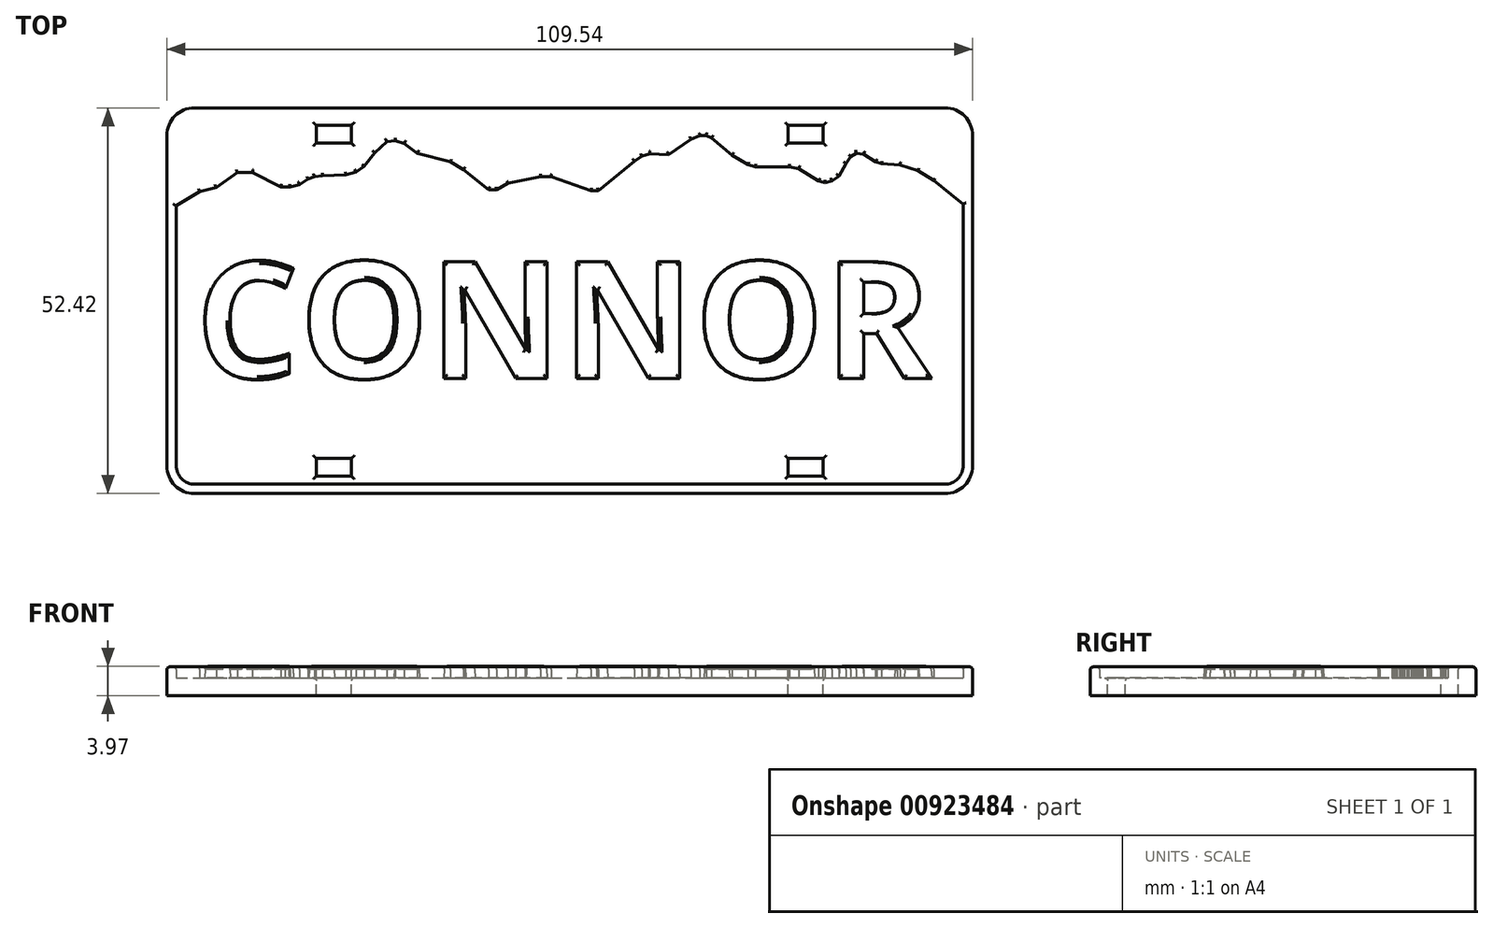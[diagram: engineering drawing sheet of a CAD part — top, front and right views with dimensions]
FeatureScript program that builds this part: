
annotation { "Feature Type Name" : "Feature", "Feature Type Description" : "" }
export const myFeature = defineFeature(function(context is Context, id is Id, definition is map)
    precondition{}
    {
        {
            var Q0;
            Q0=qCreatedBy(makeId("Top.planeOp"),FACE);
            var sketch = newSketch(context, id + "F0", { "sketchPlane" : qUnion([Q0])});
            skLineSegment(sketch, "E0", {"start": v(54.77, -22.46) * mm, "end": v(54.77, 22.46) * mm});
            skArc(sketch, "E1", {"start": v(54.77, 22.46) * mm, "mid": v(53.68, 25.11) * mm, "end": v(51.02, 26.21) * mm});
            skLineSegment(sketch, "E2", {"start": v(51.02, 26.21) * mm, "end": v(-51.02, 26.21) * mm});
            skArc(sketch, "E3", {"start": v(-51.02, 26.21) * mm, "mid": v(-53.68, 25.11) * mm, "end": v(-54.77, 22.46) * mm});
            skLineSegment(sketch, "E4", {"start": v(-54.77, 22.46) * mm, "end": v(-54.77, -22.46) * mm});
            skArc(sketch, "E5", {"start": v(-54.77, -22.46) * mm, "mid": v(-53.54, -25.24) * mm, "end": v(-50.64, -26.2) * mm});
            skLineSegment(sketch, "E6", {"start": v(-50.64, -26.2) * mm, "end": v(51.04, -26.2) * mm});
            skArc(sketch, "E7", {"start": v(51.02, -26.21) * mm, "mid": v(53.68, -25.11) * mm, "end": v(54.77, -22.46) * mm});
            skLineSegment(sketch, "E8", {"start": v(-54.77, 12.13) * mm, "end": v(-50.31, 14.84) * mm});
            skLineSegment(sketch, "E9", {"start": v(-50.31, 14.84) * mm, "end": v(-48.06, 15.4) * mm});
            skLineSegment(sketch, "E10", {"start": v(-48.06, 15.4) * mm, "end": v(-45.2, 17.44) * mm});
            skLineSegment(sketch, "E11", {"start": v(-45.2, 17.44) * mm, "end": v(-43.14, 17.44) * mm});
            skLineSegment(sketch, "E12", {"start": v(-43.14, 17.44) * mm, "end": v(-39.3, 15.5) * mm});
            skLineSegment(sketch, "E13", {"start": v(-39.3, 15.5) * mm, "end": v(-38.03, 15.49) * mm});
            skLineSegment(sketch, "E14", {"start": v(-38.03, 15.49) * mm, "end": v(-36.75, 15.8) * mm});
            skLineSegment(sketch, "E15", {"start": v(-36.75, 15.8) * mm, "end": v(-35.57, 16.54) * mm});
            skLineSegment(sketch, "E16", {"start": v(-35.57, 16.54) * mm, "end": v(-34.73, 16.88) * mm});
            skLineSegment(sketch, "E17", {"start": v(-34.73, 16.88) * mm, "end": v(-33.6, 17.01) * mm});
            skLineSegment(sketch, "E18", {"start": v(-33.6, 17.01) * mm, "end": v(-30.43, 17.11) * mm});
            skLineSegment(sketch, "E19", {"start": v(-29.05, 17.5) * mm, "end": v(-27.98, 18.27) * mm});
            skLineSegment(sketch, "E20", {"start": v(-27.98, 18.27) * mm, "end": v(-26.53, 20.14) * mm});
            skLineSegment(sketch, "E21", {"start": v(-26.53, 20.14) * mm, "end": v(-24.88, 21.63) * mm});
            skLineSegment(sketch, "E22", {"start": v(-24.88, 21.63) * mm, "end": v(-23.73, 21.77) * mm});
            skLineSegment(sketch, "E23", {"start": v(-22.5, 21.4) * mm, "end": v(-20.72, 20.04) * mm});
            skLineSegment(sketch, "E24", {"start": v(-16.23, 18.87) * mm, "end": v(-14.45, 17.85) * mm});
            skLineSegment(sketch, "E25", {"start": v(-14.45, 17.85) * mm, "end": v(-11.02, 15.1) * mm});
            skLineSegment(sketch, "E26", {"start": v(-11.02, 15.1) * mm, "end": v(-9.93, 15.1) * mm});
            skLineSegment(sketch, "E27", {"start": v(-9.93, 15.1) * mm, "end": v(-8.4, 15.96) * mm});
            skLineSegment(sketch, "E28", {"start": v(-8.4, 15.96) * mm, "end": v(-3.94, 16.85) * mm});
            skLineSegment(sketch, "E29", {"start": v(-3.94, 16.85) * mm, "end": v(-2.54, 16.85) * mm});
            skLineSegment(sketch, "E30", {"start": v(-2.54, 16.85) * mm, "end": v(2.9, 14.97) * mm});
            skLineSegment(sketch, "E31", {"start": v(2.9, 14.97) * mm, "end": v(3.92, 14.97) * mm});
            skLineSegment(sketch, "E32", {"start": v(3.92, 14.97) * mm, "end": v(8.8, 18.97) * mm});
            skLineSegment(sketch, "E33", {"start": v(8.8, 18.97) * mm, "end": v(9.82, 19.64) * mm});
            skLineSegment(sketch, "E34", {"start": v(9.82, 19.64) * mm, "end": v(10.9, 19.97) * mm});
            skLineSegment(sketch, "E35", {"start": v(10.9, 19.97) * mm, "end": v(13.43, 19.86) * mm});
            skLineSegment(sketch, "E36", {"start": v(16.5, 21.96) * mm, "end": v(17.71, 22.42) * mm});
            skLineSegment(sketch, "E37", {"start": v(17.71, 22.42) * mm, "end": v(18.56, 22.45) * mm});
            skLineSegment(sketch, "E38", {"start": v(18.56, 22.45) * mm, "end": v(19.28, 22.13) * mm});
            skLineSegment(sketch, "E39", {"start": v(19.28, 22.13) * mm, "end": v(22.05, 19.8) * mm});
            skLineSegment(sketch, "E40", {"start": v(22.05, 19.8) * mm, "end": v(24.2, 18.5) * mm});
            skLineSegment(sketch, "E41", {"start": v(24.2, 18.5) * mm, "end": v(25.23, 18.2) * mm});
            skLineSegment(sketch, "E42", {"start": v(25.23, 18.2) * mm, "end": v(29.85, 18.2) * mm});
            skLineSegment(sketch, "E43", {"start": v(29.85, 18.2) * mm, "end": v(31.13, 17.95) * mm});
            skLineSegment(sketch, "E44", {"start": v(31.13, 17.95) * mm, "end": v(33.84, 16.27) * mm});
            skLineSegment(sketch, "E45", {"start": v(33.84, 16.27) * mm, "end": v(34.73, 16.06) * mm});
            skLineSegment(sketch, "E46", {"start": v(34.73, 16.06) * mm, "end": v(35.67, 16.3) * mm});
            skLineSegment(sketch, "E47", {"start": v(35.67, 16.3) * mm, "end": v(36.58, 16.95) * mm});
            skLineSegment(sketch, "E48", {"start": v(36.58, 16.95) * mm, "end": v(37.58, 18.67) * mm});
            skLineSegment(sketch, "E49", {"start": v(38.22, 19.58) * mm, "end": v(38.96, 20.06) * mm});
            skLineSegment(sketch, "E50", {"start": v(38.96, 20.06) * mm, "end": v(39.94, 19.92) * mm});
            skLineSegment(sketch, "E51", {"start": v(41.58, 18.88) * mm, "end": v(42.4, 18.61) * mm});
            skLineSegment(sketch, "E52", {"start": v(42.4, 18.61) * mm, "end": v(44.9, 18.47) * mm});
            skLineSegment(sketch, "E53", {"start": v(44.9, 18.47) * mm, "end": v(47.31, 17.68) * mm});
            skLineSegment(sketch, "E54", {"start": v(47.31, 17.68) * mm, "end": v(49.47, 16.33) * mm});
            skLineSegment(sketch, "E55", {"start": v(49.47, 16.33) * mm, "end": v(51.88, 14.42) * mm});
            skLineSegment(sketch, "E56", {"start": v(51.88, 14.42) * mm, "end": v(53.78, 12.92) * mm});
            skLineSegment(sketch, "E57", {"start": v(53.78, 12.92) * mm, "end": v(54.77, 12.06) * mm});
            skLineSegment(sketch, "E58", {"start": v(-20.72, 20.04) * mm, "end": v(-16.23, 18.87) * mm});
            skLineSegment(sketch, "E59", {"start": v(16.5, 21.96) * mm, "end": v(13.43, 19.86) * mm});
            skLineSegment(sketch, "E60", {"start": v(-22.5, 21.4) * mm, "end": v(-23.73, 21.77) * mm});
            skLineSegment(sketch, "E61", {"start": v(-29.05, 17.5) * mm, "end": v(-30.43, 17.11) * mm});
            skLineSegment(sketch, "E62", {"start": v(37.58, 18.67) * mm, "end": v(38.22, 19.58) * mm});
            skLineSegment(sketch, "E63", {"start": v(41.58, 18.88) * mm, "end": v(39.94, 19.92) * mm});
            skSolve(sketch);
        }
        {
            var Q0;
            Q0=qCreatedBy(makeId("Top.planeOp"),FACE);
            var sketch = newSketch(context, id + "F1", { "sketchPlane" : qUnion([Q0])});
            skLineSegment(sketch, "E64", {"start": v(54.77, -22.46) * mm, "end": v(54.77, 22.46) * mm});
            skArc(sketch, "E65", {"start": v(54.77, 22.46) * mm, "mid": v(53.68, 25.11) * mm, "end": v(51.02, 26.21) * mm});
            skLineSegment(sketch, "E66", {"start": v(51.02, 26.21) * mm, "end": v(-51.02, 26.21) * mm});
            skArc(sketch, "E67", {"start": v(-51.02, 26.21) * mm, "mid": v(-53.68, 25.11) * mm, "end": v(-54.77, 22.46) * mm});
            skLineSegment(sketch, "E68", {"start": v(-54.77, 22.46) * mm, "end": v(-54.77, -22.46) * mm});
            skArc(sketch, "E69", {"start": v(-54.77, -22.46) * mm, "mid": v(-53.68, -25.11) * mm, "end": v(-51.02, -26.21) * mm});
            skLineSegment(sketch, "E70", {"start": v(-51.02, -26.21) * mm, "end": v(51.02, -26.21) * mm});
            skArc(sketch, "E71", {"start": v(51.02, -26.21) * mm, "mid": v(53.68, -25.11) * mm, "end": v(54.77, -22.46) * mm});
            skLineSegment(sketch, "E72.0", {"start": v(50.96, 24.94) * mm, "end": v(-50.96, 24.94) * mm, "construction": true});
            skLineSegment(sketch, "E72.1", {"start": v(53.5, -22.4) * mm, "end": v(53.5, 22.4) * mm, "construction": true});
            skLineSegment(sketch, "E72.2", {"start": v(-50.96, -24.94) * mm, "end": v(50.96, -24.94) * mm, "construction": true});
            skLineSegment(sketch, "E72.3", {"start": v(-53.5, 22.4) * mm, "end": v(-53.5, -22.4) * mm, "construction": true});
            skPoint(sketch, "E73.visualSharp", {"position": v(-53.5, 24.94) * mm});
            skArc(sketch, "E73.filletArc", {"start": v(-50.96, 24.94) * mm, "mid": v(-52.76, 24.2) * mm, "end": v(-53.5, 22.4) * mm, "construction": true});
            skPoint(sketch, "E74.visualSharp", {"position": v(-53.5, -24.94) * mm});
            skArc(sketch, "E74.filletArc", {"start": v(-53.5, -22.4) * mm, "mid": v(-52.76, -24.2) * mm, "end": v(-50.96, -24.94) * mm, "construction": true});
            skPoint(sketch, "E75.visualSharp", {"position": v(53.5, -24.94) * mm});
            skArc(sketch, "E75.filletArc", {"start": v(50.96, -24.94) * mm, "mid": v(52.76, -24.2) * mm, "end": v(53.5, -22.4) * mm, "construction": true});
            skPoint(sketch, "E76.visualSharp", {"position": v(53.5, 24.94) * mm});
            skArc(sketch, "E76.filletArc", {"start": v(53.5, 22.4) * mm, "mid": v(52.76, 24.2) * mm, "end": v(50.96, 24.94) * mm, "construction": true});
            skSolve(sketch);
        }
        {
            var Q0;
            {var subQ3=sQuery(id+"F0.wireOp",EDGE,"E1");Q0=makeQuery(id+"F0.imprint","IMPRINT",FACE,{"disambiguationData":[TD([[makeQuery(id+"F0.imprint","IMPRINT",EDGE,{"derivedFrom":subQ3}),1.0]])]});}
            extrude(context, id + "F2", {"entities" : qUnion([Q0]), "depth" : 1.52 * mm, "offsetDistance" : 25.4 * mm});
        }
        {
            var Q0;
            Q0=qSketchRegion(id+"F1",true);
            extrude(context, id + "F3", {"entities" : qUnion([Q0]), "operationType" : NewBodyOperationType.ADD, "oppositeDirection" : true, "depth" : 2.38 * mm, "offsetDistance" : 25.4 * mm});
        }
        {
            var Q0;
            {var subQ58=sQuery(id+"F0.wireOp",EDGE,"E0");var subQ59=sQuery(id+"F1.wireOp",EDGE,"E64");var subQ60=sQuery(id+"F1.wireOp",EDGE,"E65");var subQ61=sQuery(id+"F1.wireOp",EDGE,"E68");var subQ62=sQuery(id+"F1.wireOp",EDGE,"E69");var subQ63=sQuery(id+"F1.wireOp",EDGE,"E70");var subQ64=sQuery(id+"F1.wireOp",EDGE,"E71");Q0=makeQuery(id+"F3.boolean.opBoolean","SPLIT",FACE,{"disambiguationData":[TD([makeQuery(id+"F2.opExtrude","SWEPT_FACE",FACE,{"disambiguationData":[OSD([subQ58])]})])],"derivedFrom":makeQuery(id+"F3.opExtrude","CAP_FACE",FACE,{"disambiguationData":[OSD([subQ59,subQ60,sQuery(id+"F1.wireOp",EDGE,"E66"),sQuery(id+"F1.wireOp",EDGE,"E67"),subQ61,subQ62,subQ63,subQ64])],"isStart":true})});}
            var sketch = newSketch(context, id + "F4", { "sketchPlane" : qUnion([Q0])});
            skLineSegment(sketch, "E77", {"start": v(54.77, -22.46) * mm, "end": v(54.77, 12.06) * mm});
            skLineSegment(sketch, "E78", {"start": v(-54.77, 12.13) * mm, "end": v(-54.77, -22.46) * mm});
            skArc(sketch, "E79", {"start": v(-54.77, -22.46) * mm, "mid": v(-53.68, -25.11) * mm, "end": v(-51.02, -26.21) * mm});
            skLineSegment(sketch, "E80", {"start": v(-51.02, -26.21) * mm, "end": v(51.02, -26.21) * mm});
            skArc(sketch, "E81", {"start": v(51.02, -26.21) * mm, "mid": v(53.68, -25.11) * mm, "end": v(54.77, -22.46) * mm});
            skLineSegment(sketch, "E82.1", {"start": v(53.5, -22.4) * mm, "end": v(53.5, 13.14) * mm});
            skLineSegment(sketch, "E82.2", {"start": v(-50.96, -24.94) * mm, "end": v(50.96, -24.94) * mm});
            skLineSegment(sketch, "E82.3", {"start": v(-53.5, 12.9) * mm, "end": v(-53.5, -22.4) * mm});
            skPoint(sketch, "E83.visualSharp", {"position": v(-53.5, 24.94) * mm});
            skPoint(sketch, "E84.visualSharp", {"position": v(-53.5, -24.94) * mm});
            skArc(sketch, "E84.filletArc", {"start": v(-53.5, -22.4) * mm, "mid": v(-52.76, -24.2) * mm, "end": v(-50.96, -24.94) * mm});
            skPoint(sketch, "E85.visualSharp", {"position": v(53.5, -24.94) * mm});
            skArc(sketch, "E85.filletArc", {"start": v(50.96, -24.94) * mm, "mid": v(52.76, -24.2) * mm, "end": v(53.5, -22.4) * mm});
            skPoint(sketch, "E86.visualSharp", {"position": v(53.5, 24.94) * mm});
            skLineSegment(sketch, "E87", {"start": v(-54.77, 12.13) * mm, "end": v(-53.5, 12.9) * mm});
            skLineSegment(sketch, "E88", {"start": v(53.5, 13.14) * mm, "end": v(53.78, 12.92) * mm});
            skLineSegment(sketch, "E89", {"start": v(53.78, 12.92) * mm, "end": v(54.77, 12.06) * mm});
            skSolve(sketch);
        }
        {
            var Q0;
            Q0=qSketchRegion(id+"F4",true);
            extrude(context, id + "F5", {"entities" : qUnion([Q0]), "operationType" : NewBodyOperationType.ADD, "depth" : 1.52 * mm, "offsetDistance" : 25.4 * mm});
        }
        {
            var Q0;
            Q0=makeQuery(id+"F5.boolean.opBoolean","MERGE",FACE,{"derivedFrom":[makeQuery(id+"F2.opExtrude","CAP_FACE",FACE,{"disambiguationData":[OSD([sQuery(id+"F0.wireOp",EDGE,"E0"),sQuery(id+"F0.wireOp",EDGE,"E1"),sQuery(id+"F0.wireOp",EDGE,"E2"),sQuery(id+"F0.wireOp",EDGE,"E3"),sQuery(id+"F0.wireOp",EDGE,"E4"),sQuery(id+"F0.wireOp",EDGE,"E8"),sQuery(id+"F0.wireOp",EDGE,"E9"),sQuery(id+"F0.wireOp",EDGE,"E10"),sQuery(id+"F0.wireOp",EDGE,"E11"),sQuery(id+"F0.wireOp",EDGE,"E12"),sQuery(id+"F0.wireOp",EDGE,"E13"),sQuery(id+"F0.wireOp",EDGE,"E14"),sQuery(id+"F0.wireOp",EDGE,"E15"),sQuery(id+"F0.wireOp",EDGE,"E16"),sQuery(id+"F0.wireOp",EDGE,"E17"),sQuery(id+"F0.wireOp",EDGE,"E18"),sQuery(id+"F0.wireOp",EDGE,"7b9f405e-0691-426e-9c9e-a5372cf0836a"),sQuery(id+"F0.wireOp",EDGE,"E19"),sQuery(id+"F0.wireOp",EDGE,"E20"),sQuery(id+"F0.wireOp",EDGE,"E21"),sQuery(id+"F0.wireOp",EDGE,"E22"),sQuery(id+"F0.wireOp",EDGE,"b3dec5b1-662c-4d50-a13c-af7b7760114a"),sQuery(id+"F0.wireOp",EDGE,"E23"),sQuery(id+"F0.wireOp",EDGE,"4d9ee76e-0833-4cdc-b1a8-2d4ce76e6521"),sQuery(id+"F0.wireOp",EDGE,"E24"),sQuery(id+"F0.wireOp",EDGE,"E25"),sQuery(id+"F0.wireOp",EDGE,"E26"),sQuery(id+"F0.wireOp",EDGE,"E27"),sQuery(id+"F0.wireOp",EDGE,"E28"),sQuery(id+"F0.wireOp",EDGE,"E29"),sQuery(id+"F0.wireOp",EDGE,"E30"),sQuery(id+"F0.wireOp",EDGE,"E31"),sQuery(id+"F0.wireOp",EDGE,"E32"),sQuery(id+"F0.wireOp",EDGE,"E33"),sQuery(id+"F0.wireOp",EDGE,"E34"),sQuery(id+"F0.wireOp",EDGE,"E35"),sQuery(id+"F0.wireOp",EDGE,"55551997-bb9e-4b94-90c5-def3cb147476"),sQuery(id+"F0.wireOp",EDGE,"E36"),sQuery(id+"F0.wireOp",EDGE,"E37"),sQuery(id+"F0.wireOp",EDGE,"E38"),sQuery(id+"F0.wireOp",EDGE,"E39"),sQuery(id+"F0.wireOp",EDGE,"E40"),sQuery(id+"F0.wireOp",EDGE,"E41"),sQuery(id+"F0.wireOp",EDGE,"E42"),sQuery(id+"F0.wireOp",EDGE,"E43"),sQuery(id+"F0.wireOp",EDGE,"E44"),sQuery(id+"F0.wireOp",EDGE,"E45"),sQuery(id+"F0.wireOp",EDGE,"E46"),sQuery(id+"F0.wireOp",EDGE,"E47"),sQuery(id+"F0.wireOp",EDGE,"E48"),sQuery(id+"F0.wireOp",EDGE,"513b7cbe-d979-4e22-b277-f3c42ccdbda1"),sQuery(id+"F0.wireOp",EDGE,"E49"),sQuery(id+"F0.wireOp",EDGE,"E50"),sQuery(id+"F0.wireOp",EDGE,"0d842e13-672c-40e3-aae4-28923e78d4e0"),sQuery(id+"F0.wireOp",EDGE,"E51"),sQuery(id+"F0.wireOp",EDGE,"E52"),sQuery(id+"F0.wireOp",EDGE,"E53"),sQuery(id+"F0.wireOp",EDGE,"E54"),sQuery(id+"F0.wireOp",EDGE,"E55"),sQuery(id+"F0.wireOp",EDGE,"E56"),sQuery(id+"F0.wireOp",EDGE,"E57")])],"isStart":false}),makeQuery(id+"F5.opExtrude","CAP_FACE",FACE,{"disambiguationData":[OSD([sQuery(id+"F4.wireOp",EDGE,"E77"),sQuery(id+"F4.wireOp",EDGE,"E78"),sQuery(id+"F4.wireOp",EDGE,"E79"),sQuery(id+"F4.wireOp",EDGE,"E80"),sQuery(id+"F4.wireOp",EDGE,"E81"),sQuery(id+"F4.wireOp",EDGE,"E82.1"),sQuery(id+"F4.wireOp",EDGE,"E82.2"),sQuery(id+"F4.wireOp",EDGE,"E82.3"),sQuery(id+"F4.wireOp",EDGE,"E84.filletArc"),sQuery(id+"F4.wireOp",EDGE,"E85.filletArc"),sQuery(id+"F4.wireOp",EDGE,"E87"),sQuery(id+"F4.wireOp",EDGE,"E88"),sQuery(id+"F4.wireOp",EDGE,"E89")])],"isStart":false})]});
            var sketch = newSketch(context, id + "F6", { "sketchPlane" : qUnion([Q0])});
            skLineSegment(sketch, "E90.bottom", {"start": v(-34.45, 23.83) * mm, "end": v(-29.7, 23.83) * mm});
            skLineSegment(sketch, "E90.top", {"start": v(-34.45, 21.45) * mm, "end": v(-29.7, 21.45) * mm});
            skLineSegment(sketch, "E90.left", {"start": v(-34.45, 23.83) * mm, "end": v(-34.45, 21.45) * mm});
            skLineSegment(sketch, "E90.right", {"start": v(-29.7, 23.83) * mm, "end": v(-29.7, 21.45) * mm});
            skLineSegment(sketch, "E91", {"start": v(0, 26.21) * mm, "end": v(0, -26.21) * mm, "construction": true});
            skLineSegment(sketch, "E92.MirrorCS", {"start": v(34.45, 23.83) * mm, "end": v(34.45, 21.45) * mm});
            skLineSegment(sketch, "E93.MirrorCS", {"start": v(29.7, 23.83) * mm, "end": v(29.7, 21.45) * mm});
            skLineSegment(sketch, "E94.MirrorCS", {"start": v(34.45, 21.45) * mm, "end": v(29.7, 21.45) * mm});
            skLineSegment(sketch, "E95.MirrorCS", {"start": v(34.45, 23.83) * mm, "end": v(29.7, 23.83) * mm});
            skLineSegment(sketch, "E96", {"start": v(0, 0) * mm, "end": v(-59.23, 0) * mm, "construction": true});
            skLineSegment(sketch, "E97", {"start": v(0, 0) * mm, "end": v(56.47, 0) * mm, "construction": true});
            skLineSegment(sketch, "E98.MirrorCS", {"start": v(-34.45, -23.83) * mm, "end": v(-29.7, -23.83) * mm});
            skLineSegment(sketch, "E99.MirrorCS", {"start": v(-34.45, -23.83) * mm, "end": v(-34.45, -21.45) * mm});
            skLineSegment(sketch, "E100.MirrorCS", {"start": v(-34.45, -21.45) * mm, "end": v(-29.7, -21.45) * mm});
            skLineSegment(sketch, "E101.MirrorCS", {"start": v(-29.7, -23.83) * mm, "end": v(-29.7, -21.45) * mm});
            skLineSegment(sketch, "E102.MirrorCS", {"start": v(29.7, -23.83) * mm, "end": v(29.7, -21.45) * mm});
            skLineSegment(sketch, "E103.MirrorCS", {"start": v(34.45, -23.83) * mm, "end": v(29.7, -23.83) * mm});
            skLineSegment(sketch, "E104.MirrorCS", {"start": v(34.45, -23.83) * mm, "end": v(34.45, -21.45) * mm});
            skLineSegment(sketch, "E105.MirrorCS", {"start": v(34.45, -21.45) * mm, "end": v(29.7, -21.45) * mm});
            skSolve(sketch);
        }
        {
            var Q0;
            Q0=qSketchRegion(id+"F6",true);
            extrude(context, id + "F7", {"entities" : qUnion([Q0]), "operationType" : NewBodyOperationType.REMOVE, "endBound" : BoundingType.THROUGH_ALL, "oppositeDirection" : true, "depth" : 25.4 * mm, "offsetDistance" : 25.4 * mm});
        }
        {
            var Q0;
            Q0=makeQuery(id+"F3.opExtrude","CAP_FACE",FACE,{"disambiguationData":[OSD([sQuery(id+"F1.wireOp",EDGE,"E64"),sQuery(id+"F1.wireOp",EDGE,"E65"),sQuery(id+"F1.wireOp",EDGE,"E66"),sQuery(id+"F1.wireOp",EDGE,"E67"),sQuery(id+"F1.wireOp",EDGE,"E68"),sQuery(id+"F1.wireOp",EDGE,"E69"),sQuery(id+"F1.wireOp",EDGE,"E70"),sQuery(id+"F1.wireOp",EDGE,"E71")])],"isStart":true});
            var sketch = newSketch(context, id + "F8", { "sketchPlane" : qUnion([Q0])});
            skText(sketch, "E106", { "text": "CONNOR", "fontName": "NotoSans-Bold.ttf"});
            const initialGuessF8  = {"E106": [-0.0509, -0.01054, 1, 0, 0.01597]};
            skSetInitialGuess(sketch, initialGuessF8);
            skSolve(sketch);
        }
        {
            var Q0;
            Q0 = qSketchRegion(id + "F8", true);
            extrude(context, id + "F9", {"entities" : qUnion([Q0]), "operationType" : NewBodyOperationType.ADD, "depth" : 1.59 * mm, "offsetDistance" : 25.4 * mm, "hasDraft" : true, "draftAngle" : 3 * degree, "draftPullDirection" : true});
        }
        {
            var Q0;
            Q0=makeQuery(id+"F5.boolean.opBoolean","MERGE",FACE,{"derivedFrom":[makeQuery(id+"F2.opExtrude","CAP_FACE",FACE,{"disambiguationData":[OSD([sQuery(id+"F0.wireOp",EDGE,"E0"),sQuery(id+"F0.wireOp",EDGE,"E1"),sQuery(id+"F0.wireOp",EDGE,"E2"),sQuery(id+"F0.wireOp",EDGE,"E3"),sQuery(id+"F0.wireOp",EDGE,"E4"),sQuery(id+"F0.wireOp",EDGE,"E8"),sQuery(id+"F0.wireOp",EDGE,"E9"),sQuery(id+"F0.wireOp",EDGE,"E10"),sQuery(id+"F0.wireOp",EDGE,"E11"),sQuery(id+"F0.wireOp",EDGE,"E12"),sQuery(id+"F0.wireOp",EDGE,"E13"),sQuery(id+"F0.wireOp",EDGE,"E14"),sQuery(id+"F0.wireOp",EDGE,"E15"),sQuery(id+"F0.wireOp",EDGE,"E16"),sQuery(id+"F0.wireOp",EDGE,"E17"),sQuery(id+"F0.wireOp",EDGE,"E18"),sQuery(id+"F0.wireOp",EDGE,"7b9f405e-0691-426e-9c9e-a5372cf0836a"),sQuery(id+"F0.wireOp",EDGE,"E19"),sQuery(id+"F0.wireOp",EDGE,"E20"),sQuery(id+"F0.wireOp",EDGE,"E21"),sQuery(id+"F0.wireOp",EDGE,"E22"),sQuery(id+"F0.wireOp",EDGE,"b3dec5b1-662c-4d50-a13c-af7b7760114a"),sQuery(id+"F0.wireOp",EDGE,"E23"),sQuery(id+"F0.wireOp",EDGE,"4d9ee76e-0833-4cdc-b1a8-2d4ce76e6521"),sQuery(id+"F0.wireOp",EDGE,"E24"),sQuery(id+"F0.wireOp",EDGE,"E25"),sQuery(id+"F0.wireOp",EDGE,"E26"),sQuery(id+"F0.wireOp",EDGE,"E27"),sQuery(id+"F0.wireOp",EDGE,"E28"),sQuery(id+"F0.wireOp",EDGE,"E29"),sQuery(id+"F0.wireOp",EDGE,"E30"),sQuery(id+"F0.wireOp",EDGE,"E31"),sQuery(id+"F0.wireOp",EDGE,"E32"),sQuery(id+"F0.wireOp",EDGE,"E33"),sQuery(id+"F0.wireOp",EDGE,"E34"),sQuery(id+"F0.wireOp",EDGE,"E35"),sQuery(id+"F0.wireOp",EDGE,"55551997-bb9e-4b94-90c5-def3cb147476"),sQuery(id+"F0.wireOp",EDGE,"E36"),sQuery(id+"F0.wireOp",EDGE,"E37"),sQuery(id+"F0.wireOp",EDGE,"E38"),sQuery(id+"F0.wireOp",EDGE,"E39"),sQuery(id+"F0.wireOp",EDGE,"E40"),sQuery(id+"F0.wireOp",EDGE,"E41"),sQuery(id+"F0.wireOp",EDGE,"E42"),sQuery(id+"F0.wireOp",EDGE,"E43"),sQuery(id+"F0.wireOp",EDGE,"E44"),sQuery(id+"F0.wireOp",EDGE,"E45"),sQuery(id+"F0.wireOp",EDGE,"E46"),sQuery(id+"F0.wireOp",EDGE,"E47"),sQuery(id+"F0.wireOp",EDGE,"E48"),sQuery(id+"F0.wireOp",EDGE,"513b7cbe-d979-4e22-b277-f3c42ccdbda1"),sQuery(id+"F0.wireOp",EDGE,"E49"),sQuery(id+"F0.wireOp",EDGE,"E50"),sQuery(id+"F0.wireOp",EDGE,"0d842e13-672c-40e3-aae4-28923e78d4e0"),sQuery(id+"F0.wireOp",EDGE,"E51"),sQuery(id+"F0.wireOp",EDGE,"E52"),sQuery(id+"F0.wireOp",EDGE,"E53"),sQuery(id+"F0.wireOp",EDGE,"E54"),sQuery(id+"F0.wireOp",EDGE,"E55"),sQuery(id+"F0.wireOp",EDGE,"E56"),sQuery(id+"F0.wireOp",EDGE,"E57")])],"isStart":false}),makeQuery(id+"F5.opExtrude","CAP_FACE",FACE,{"disambiguationData":[OSD([sQuery(id+"F4.wireOp",EDGE,"E77"),sQuery(id+"F4.wireOp",EDGE,"E78"),sQuery(id+"F4.wireOp",EDGE,"E79"),sQuery(id+"F4.wireOp",EDGE,"E80"),sQuery(id+"F4.wireOp",EDGE,"E81"),sQuery(id+"F4.wireOp",EDGE,"E82.1"),sQuery(id+"F4.wireOp",EDGE,"E82.2"),sQuery(id+"F4.wireOp",EDGE,"E82.3"),sQuery(id+"F4.wireOp",EDGE,"E84.filletArc"),sQuery(id+"F4.wireOp",EDGE,"E85.filletArc"),sQuery(id+"F4.wireOp",EDGE,"E87"),sQuery(id+"F4.wireOp",EDGE,"E88"),sQuery(id+"F4.wireOp",EDGE,"E89")])],"isStart":false})]});
            var Q1;
            {var subQ0=sQuery(id+"F1.wireOp",EDGE,"E64");var subQ1=sQuery(id+"F1.wireOp",EDGE,"E68");var subQ2=sQuery(id+"F1.wireOp",EDGE,"E69");var subQ3=sQuery(id+"F1.wireOp",EDGE,"E70");var subQ4=sQuery(id+"F1.wireOp",EDGE,"E71");Q1=makeQuery(id+"F7.boolean.opBoolean","INTERSECT",EDGE,{"derivedFrom":[makeQuery(id+"F3.boolean.opBoolean","SPLIT",FACE,{"disambiguationData":[TD([makeQuery(id+"F2.opExtrude","SWEPT_FACE",FACE,{"disambiguationData":[OSD([sQuery(id+"F0.wireOp",EDGE,"E0")])]})])],"derivedFrom":makeQuery(id+"F3.opExtrude","CAP_FACE",FACE,{"disambiguationData":[OSD([subQ0,sQuery(id+"F1.wireOp",EDGE,"E65"),sQuery(id+"F1.wireOp",EDGE,"E66"),sQuery(id+"F1.wireOp",EDGE,"E67"),subQ1,subQ2,subQ3,subQ4])],"isStart":true})}),makeQuery(id+"F7.opExtrude","SWEPT_FACE",FACE,{"disambiguationData":[OSD([sQuery(id+"F6.wireOp",EDGE,"E100.MirrorCS")])]})]});}
            var Q2;
            {var subQ0=sQuery(id+"F1.wireOp",EDGE,"E64");var subQ1=sQuery(id+"F1.wireOp",EDGE,"E68");var subQ2=sQuery(id+"F1.wireOp",EDGE,"E69");var subQ3=sQuery(id+"F1.wireOp",EDGE,"E70");var subQ4=sQuery(id+"F1.wireOp",EDGE,"E71");Q2=makeQuery(id+"F7.boolean.opBoolean","INTERSECT",EDGE,{"derivedFrom":[makeQuery(id+"F3.boolean.opBoolean","SPLIT",FACE,{"disambiguationData":[TD([makeQuery(id+"F2.opExtrude","SWEPT_FACE",FACE,{"disambiguationData":[OSD([sQuery(id+"F0.wireOp",EDGE,"E0")])]})])],"derivedFrom":makeQuery(id+"F3.opExtrude","CAP_FACE",FACE,{"disambiguationData":[OSD([subQ0,sQuery(id+"F1.wireOp",EDGE,"E65"),sQuery(id+"F1.wireOp",EDGE,"E66"),sQuery(id+"F1.wireOp",EDGE,"E67"),subQ1,subQ2,subQ3,subQ4])],"isStart":true})}),makeQuery(id+"F7.opExtrude","SWEPT_FACE",FACE,{"disambiguationData":[OSD([sQuery(id+"F6.wireOp",EDGE,"E99.MirrorCS")])]})]});}
            var Q3;
            {var subQ0=sQuery(id+"F1.wireOp",EDGE,"E64");var subQ1=sQuery(id+"F1.wireOp",EDGE,"E68");var subQ2=sQuery(id+"F1.wireOp",EDGE,"E69");var subQ3=sQuery(id+"F1.wireOp",EDGE,"E70");var subQ4=sQuery(id+"F1.wireOp",EDGE,"E71");Q3=makeQuery(id+"F7.boolean.opBoolean","INTERSECT",EDGE,{"derivedFrom":[makeQuery(id+"F3.boolean.opBoolean","SPLIT",FACE,{"disambiguationData":[TD([makeQuery(id+"F2.opExtrude","SWEPT_FACE",FACE,{"disambiguationData":[OSD([sQuery(id+"F0.wireOp",EDGE,"E0")])]})])],"derivedFrom":makeQuery(id+"F3.opExtrude","CAP_FACE",FACE,{"disambiguationData":[OSD([subQ0,sQuery(id+"F1.wireOp",EDGE,"E65"),sQuery(id+"F1.wireOp",EDGE,"E66"),sQuery(id+"F1.wireOp",EDGE,"E67"),subQ1,subQ2,subQ3,subQ4])],"isStart":true})}),makeQuery(id+"F7.opExtrude","SWEPT_FACE",FACE,{"disambiguationData":[OSD([sQuery(id+"F6.wireOp",EDGE,"E98.MirrorCS")])]})]});}
            var Q4;
            {var subQ0=sQuery(id+"F1.wireOp",EDGE,"E64");var subQ1=sQuery(id+"F1.wireOp",EDGE,"E68");var subQ2=sQuery(id+"F1.wireOp",EDGE,"E69");var subQ3=sQuery(id+"F1.wireOp",EDGE,"E70");var subQ4=sQuery(id+"F1.wireOp",EDGE,"E71");Q4=makeQuery(id+"F7.boolean.opBoolean","INTERSECT",EDGE,{"derivedFrom":[makeQuery(id+"F3.boolean.opBoolean","SPLIT",FACE,{"disambiguationData":[TD([makeQuery(id+"F2.opExtrude","SWEPT_FACE",FACE,{"disambiguationData":[OSD([sQuery(id+"F0.wireOp",EDGE,"E0")])]})])],"derivedFrom":makeQuery(id+"F3.opExtrude","CAP_FACE",FACE,{"disambiguationData":[OSD([subQ0,sQuery(id+"F1.wireOp",EDGE,"E65"),sQuery(id+"F1.wireOp",EDGE,"E66"),sQuery(id+"F1.wireOp",EDGE,"E67"),subQ1,subQ2,subQ3,subQ4])],"isStart":true})}),makeQuery(id+"F7.opExtrude","SWEPT_FACE",FACE,{"disambiguationData":[OSD([sQuery(id+"F6.wireOp",EDGE,"E101.MirrorCS")])]})]});}
            var Q5;
            {var subQ0=sQuery(id+"F1.wireOp",EDGE,"E64");var subQ1=sQuery(id+"F1.wireOp",EDGE,"E68");var subQ2=sQuery(id+"F1.wireOp",EDGE,"E69");var subQ3=sQuery(id+"F1.wireOp",EDGE,"E70");var subQ4=sQuery(id+"F1.wireOp",EDGE,"E71");Q5=makeQuery(id+"F7.boolean.opBoolean","INTERSECT",EDGE,{"derivedFrom":[makeQuery(id+"F3.boolean.opBoolean","SPLIT",FACE,{"disambiguationData":[TD([makeQuery(id+"F2.opExtrude","SWEPT_FACE",FACE,{"disambiguationData":[OSD([sQuery(id+"F0.wireOp",EDGE,"E0")])]})])],"derivedFrom":makeQuery(id+"F3.opExtrude","CAP_FACE",FACE,{"disambiguationData":[OSD([subQ0,sQuery(id+"F1.wireOp",EDGE,"E65"),sQuery(id+"F1.wireOp",EDGE,"E66"),sQuery(id+"F1.wireOp",EDGE,"E67"),subQ1,subQ2,subQ3,subQ4])],"isStart":true})}),makeQuery(id+"F7.opExtrude","SWEPT_FACE",FACE,{"disambiguationData":[OSD([sQuery(id+"F6.wireOp",EDGE,"E102.MirrorCS")])]})]});}
            var Q6;
            {var subQ0=sQuery(id+"F1.wireOp",EDGE,"E64");var subQ1=sQuery(id+"F1.wireOp",EDGE,"E68");var subQ2=sQuery(id+"F1.wireOp",EDGE,"E69");var subQ3=sQuery(id+"F1.wireOp",EDGE,"E70");var subQ4=sQuery(id+"F1.wireOp",EDGE,"E71");Q6=makeQuery(id+"F7.boolean.opBoolean","INTERSECT",EDGE,{"derivedFrom":[makeQuery(id+"F3.boolean.opBoolean","SPLIT",FACE,{"disambiguationData":[TD([makeQuery(id+"F2.opExtrude","SWEPT_FACE",FACE,{"disambiguationData":[OSD([sQuery(id+"F0.wireOp",EDGE,"E0")])]})])],"derivedFrom":makeQuery(id+"F3.opExtrude","CAP_FACE",FACE,{"disambiguationData":[OSD([subQ0,sQuery(id+"F1.wireOp",EDGE,"E65"),sQuery(id+"F1.wireOp",EDGE,"E66"),sQuery(id+"F1.wireOp",EDGE,"E67"),subQ1,subQ2,subQ3,subQ4])],"isStart":true})}),makeQuery(id+"F7.opExtrude","SWEPT_FACE",FACE,{"disambiguationData":[OSD([sQuery(id+"F6.wireOp",EDGE,"E105.MirrorCS")])]})]});}
            var Q7;
            {var subQ0=sQuery(id+"F1.wireOp",EDGE,"E64");var subQ1=sQuery(id+"F1.wireOp",EDGE,"E68");var subQ2=sQuery(id+"F1.wireOp",EDGE,"E69");var subQ3=sQuery(id+"F1.wireOp",EDGE,"E70");var subQ4=sQuery(id+"F1.wireOp",EDGE,"E71");Q7=makeQuery(id+"F7.boolean.opBoolean","INTERSECT",EDGE,{"derivedFrom":[makeQuery(id+"F3.boolean.opBoolean","SPLIT",FACE,{"disambiguationData":[TD([makeQuery(id+"F2.opExtrude","SWEPT_FACE",FACE,{"disambiguationData":[OSD([sQuery(id+"F0.wireOp",EDGE,"E0")])]})])],"derivedFrom":makeQuery(id+"F3.opExtrude","CAP_FACE",FACE,{"disambiguationData":[OSD([subQ0,sQuery(id+"F1.wireOp",EDGE,"E65"),sQuery(id+"F1.wireOp",EDGE,"E66"),sQuery(id+"F1.wireOp",EDGE,"E67"),subQ1,subQ2,subQ3,subQ4])],"isStart":true})}),makeQuery(id+"F7.opExtrude","SWEPT_FACE",FACE,{"disambiguationData":[OSD([sQuery(id+"F6.wireOp",EDGE,"E104.MirrorCS")])]})]});}
            var Q8;
            {var subQ0=sQuery(id+"F1.wireOp",EDGE,"E64");var subQ1=sQuery(id+"F1.wireOp",EDGE,"E68");var subQ2=sQuery(id+"F1.wireOp",EDGE,"E69");var subQ3=sQuery(id+"F1.wireOp",EDGE,"E70");var subQ4=sQuery(id+"F1.wireOp",EDGE,"E71");Q8=makeQuery(id+"F7.boolean.opBoolean","INTERSECT",EDGE,{"derivedFrom":[makeQuery(id+"F3.boolean.opBoolean","SPLIT",FACE,{"disambiguationData":[TD([makeQuery(id+"F2.opExtrude","SWEPT_FACE",FACE,{"disambiguationData":[OSD([sQuery(id+"F0.wireOp",EDGE,"E0")])]})])],"derivedFrom":makeQuery(id+"F3.opExtrude","CAP_FACE",FACE,{"disambiguationData":[OSD([subQ0,sQuery(id+"F1.wireOp",EDGE,"E65"),sQuery(id+"F1.wireOp",EDGE,"E66"),sQuery(id+"F1.wireOp",EDGE,"E67"),subQ1,subQ2,subQ3,subQ4])],"isStart":true})}),makeQuery(id+"F7.opExtrude","SWEPT_FACE",FACE,{"disambiguationData":[OSD([sQuery(id+"F6.wireOp",EDGE,"E103.MirrorCS")])]})]});}
            var Q9;
            Q9=makeQuery(id+"F9.opExtrude","CAP_FACE",FACE,{"disambiguationData":[OSD([sQuery(id+"F8.wireOp",EDGE,"E106.sketch_text.stroke-0"),sQuery(id+"F8.wireOp",EDGE,"E106.sketch_text.stroke-1"),sQuery(id+"F8.wireOp",EDGE,"E106.sketch_text.stroke-2"),sQuery(id+"F8.wireOp",EDGE,"E106.sketch_text.stroke-3"),sQuery(id+"F8.wireOp",EDGE,"E106.sketch_text.stroke-4"),sQuery(id+"F8.wireOp",EDGE,"E106.sketch_text.stroke-5"),sQuery(id+"F8.wireOp",EDGE,"E106.sketch_text.stroke-6"),sQuery(id+"F8.wireOp",EDGE,"E106.sketch_text.stroke-7"),sQuery(id+"F8.wireOp",EDGE,"E106.sketch_text.stroke-8"),sQuery(id+"F8.wireOp",EDGE,"E106.sketch_text.stroke-9"),sQuery(id+"F8.wireOp",EDGE,"E106.sketch_text.stroke-10"),sQuery(id+"F8.wireOp",EDGE,"E106.sketch_text.stroke-11"),sQuery(id+"F8.wireOp",EDGE,"E106.sketch_text.stroke-12"),sQuery(id+"F8.wireOp",EDGE,"E106.sketch_text.stroke-13"),sQuery(id+"F8.wireOp",EDGE,"E106.sketch_text.stroke-14")])],"isStart":false});
            var Q10;
            Q10=makeQuery(id+"F9.opExtrude","CAP_FACE",FACE,{"disambiguationData":[OSD([sQuery(id+"F8.wireOp",EDGE,"E106.sketch_text.stroke-15"),sQuery(id+"F8.wireOp",EDGE,"E106.sketch_text.stroke-16"),sQuery(id+"F8.wireOp",EDGE,"E106.sketch_text.stroke-17"),sQuery(id+"F8.wireOp",EDGE,"E106.sketch_text.stroke-18"),sQuery(id+"F8.wireOp",EDGE,"E106.sketch_text.stroke-19"),sQuery(id+"F8.wireOp",EDGE,"E106.sketch_text.stroke-20"),sQuery(id+"F8.wireOp",EDGE,"E106.sketch_text.stroke-21"),sQuery(id+"F8.wireOp",EDGE,"E106.sketch_text.stroke-22"),sQuery(id+"F8.wireOp",EDGE,"E106.sketch_text.stroke-23"),sQuery(id+"F8.wireOp",EDGE,"E106.sketch_text.stroke-24"),sQuery(id+"F8.wireOp",EDGE,"E106.sketch_text.stroke-25"),sQuery(id+"F8.wireOp",EDGE,"E106.sketch_text.stroke-26"),sQuery(id+"F8.wireOp",EDGE,"E106.sketch_text.stroke-27"),sQuery(id+"F8.wireOp",EDGE,"E106.sketch_text.stroke-28")])],"isStart":false});
            var Q11;
            Q11=makeQuery(id+"F9.opExtrude","CAP_FACE",FACE,{"disambiguationData":[OSD([sQuery(id+"F8.wireOp",EDGE,"E106.sketch_text.stroke-29"),sQuery(id+"F8.wireOp",EDGE,"E106.sketch_text.stroke-30"),sQuery(id+"F8.wireOp",EDGE,"E106.sketch_text.stroke-31"),sQuery(id+"F8.wireOp",EDGE,"E106.sketch_text.stroke-32"),sQuery(id+"F8.wireOp",EDGE,"E106.sketch_text.stroke-33"),sQuery(id+"F8.wireOp",EDGE,"E106.sketch_text.stroke-34"),sQuery(id+"F8.wireOp",EDGE,"E106.sketch_text.stroke-35"),sQuery(id+"F8.wireOp",EDGE,"E106.sketch_text.stroke-36"),sQuery(id+"F8.wireOp",EDGE,"E106.sketch_text.stroke-37"),sQuery(id+"F8.wireOp",EDGE,"E106.sketch_text.stroke-38"),sQuery(id+"F8.wireOp",EDGE,"E106.sketch_text.stroke-39"),sQuery(id+"F8.wireOp",EDGE,"E106.sketch_text.stroke-40"),sQuery(id+"F8.wireOp",EDGE,"E106.sketch_text.stroke-41"),sQuery(id+"F8.wireOp",EDGE,"E106.sketch_text.stroke-42")])],"isStart":false});
            var Q12;
            Q12=makeQuery(id+"F9.opExtrude","CAP_FACE",FACE,{"disambiguationData":[OSD([sQuery(id+"F8.wireOp",EDGE,"E106.sketch_text.stroke-57"),sQuery(id+"F8.wireOp",EDGE,"E106.sketch_text.stroke-58"),sQuery(id+"F8.wireOp",EDGE,"E106.sketch_text.stroke-59"),sQuery(id+"F8.wireOp",EDGE,"E106.sketch_text.stroke-60"),sQuery(id+"F8.wireOp",EDGE,"E106.sketch_text.stroke-61"),sQuery(id+"F8.wireOp",EDGE,"E106.sketch_text.stroke-62"),sQuery(id+"F8.wireOp",EDGE,"E106.sketch_text.stroke-63"),sQuery(id+"F8.wireOp",EDGE,"E106.sketch_text.stroke-64"),sQuery(id+"F8.wireOp",EDGE,"E106.sketch_text.stroke-65"),sQuery(id+"F8.wireOp",EDGE,"E106.sketch_text.stroke-66"),sQuery(id+"F8.wireOp",EDGE,"E106.sketch_text.stroke-67"),sQuery(id+"F8.wireOp",EDGE,"E106.sketch_text.stroke-68"),sQuery(id+"F8.wireOp",EDGE,"E106.sketch_text.stroke-69"),sQuery(id+"F8.wireOp",EDGE,"E106.sketch_text.stroke-70")])],"isStart":false});
            var Q13;
            Q13=makeQuery(id+"F9.opExtrude","CAP_FACE",FACE,{"disambiguationData":[OSD([sQuery(id+"F8.wireOp",EDGE,"E106.sketch_text.stroke-71"),sQuery(id+"F8.wireOp",EDGE,"E106.sketch_text.stroke-72"),sQuery(id+"F8.wireOp",EDGE,"E106.sketch_text.stroke-73"),sQuery(id+"F8.wireOp",EDGE,"E106.sketch_text.stroke-74"),sQuery(id+"F8.wireOp",EDGE,"E106.sketch_text.stroke-75"),sQuery(id+"F8.wireOp",EDGE,"E106.sketch_text.stroke-76"),sQuery(id+"F8.wireOp",EDGE,"E106.sketch_text.stroke-77"),sQuery(id+"F8.wireOp",EDGE,"E106.sketch_text.stroke-78"),sQuery(id+"F8.wireOp",EDGE,"E106.sketch_text.stroke-79"),sQuery(id+"F8.wireOp",EDGE,"E106.sketch_text.stroke-80"),sQuery(id+"F8.wireOp",EDGE,"E106.sketch_text.stroke-81"),sQuery(id+"F8.wireOp",EDGE,"E106.sketch_text.stroke-82"),sQuery(id+"F8.wireOp",EDGE,"E106.sketch_text.stroke-83"),sQuery(id+"F8.wireOp",EDGE,"E106.sketch_text.stroke-84"),sQuery(id+"F8.wireOp",EDGE,"E106.sketch_text.stroke-85"),sQuery(id+"F8.wireOp",EDGE,"E106.sketch_text.stroke-86"),sQuery(id+"F8.wireOp",EDGE,"E106.sketch_text.stroke-87"),sQuery(id+"F8.wireOp",EDGE,"E106.sketch_text.stroke-88"),sQuery(id+"F8.wireOp",EDGE,"E106.sketch_text.stroke-89")])],"isStart":false});
            var Q14;
            Q14=makeQuery(id+"F9.opExtrude","CAP_FACE",FACE,{"disambiguationData":[OSD([sQuery(id+"F8.wireOp",EDGE,"E106.sketch_text.stroke-43"),sQuery(id+"F8.wireOp",EDGE,"E106.sketch_text.stroke-44"),sQuery(id+"F8.wireOp",EDGE,"E106.sketch_text.stroke-45"),sQuery(id+"F8.wireOp",EDGE,"E106.sketch_text.stroke-46"),sQuery(id+"F8.wireOp",EDGE,"E106.sketch_text.stroke-47"),sQuery(id+"F8.wireOp",EDGE,"E106.sketch_text.stroke-48"),sQuery(id+"F8.wireOp",EDGE,"E106.sketch_text.stroke-49"),sQuery(id+"F8.wireOp",EDGE,"E106.sketch_text.stroke-50"),sQuery(id+"F8.wireOp",EDGE,"E106.sketch_text.stroke-51"),sQuery(id+"F8.wireOp",EDGE,"E106.sketch_text.stroke-52"),sQuery(id+"F8.wireOp",EDGE,"E106.sketch_text.stroke-53"),sQuery(id+"F8.wireOp",EDGE,"E106.sketch_text.stroke-54"),sQuery(id+"F8.wireOp",EDGE,"E106.sketch_text.stroke-55"),sQuery(id+"F8.wireOp",EDGE,"E106.sketch_text.stroke-56")])],"isStart":false});
            fillet(context, id + "F10", {"entities" : qUnion([Q0, Q1, Q2, Q3, Q4, Q5, Q6, Q7, Q8, Q9, Q10, Q11, Q12, Q13, Q14]), "radius" : 0.38 * mm, "tangentPropagation" : true, "allowEdgeOverflow" : false});
        }
    });
